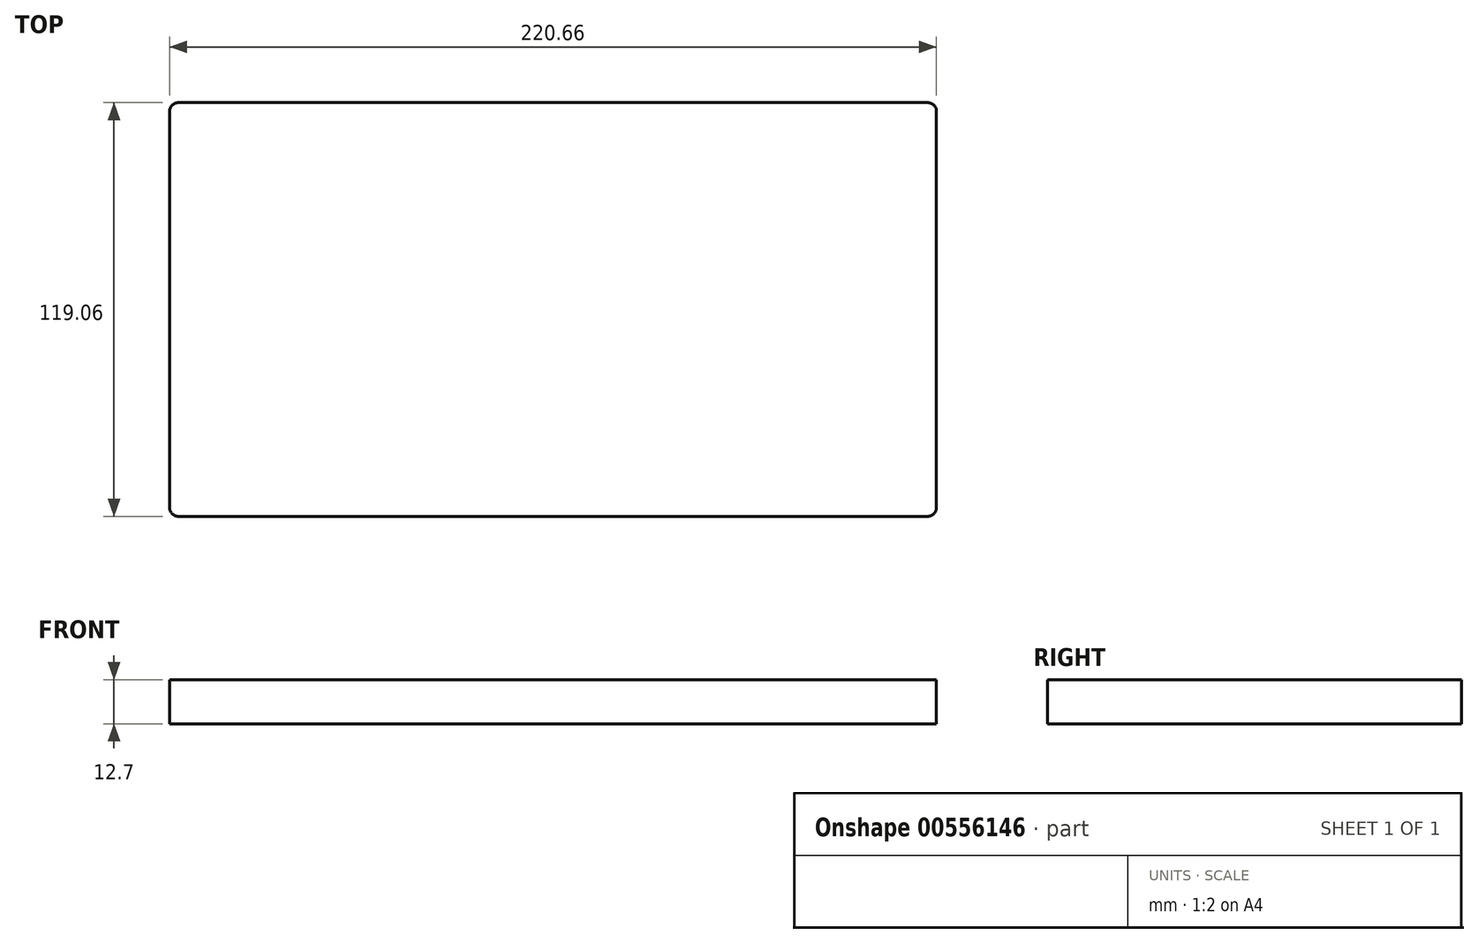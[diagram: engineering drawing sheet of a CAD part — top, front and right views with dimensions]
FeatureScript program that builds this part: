
annotation { "Feature Type Name" : "Feature", "Feature Type Description" : "" }
export const myFeature = defineFeature(function(context is Context, id is Id, definition is map)
    precondition{}
    {
        {
            var Q0;
            Q0=qCreatedBy(makeId("Top.planeOp"),FACE);
            var sketch = newSketch(context, id + "F0", { "sketchPlane" : qUnion([Q0])});
            skLineSegment(sketch, "E0.bottom", {"start": v(-107.79, 59.53) * mm, "end": v(107.79, 59.53) * mm});
            skLineSegment(sketch, "E0.top", {"start": v(-107.79, -59.53) * mm, "end": v(107.79, -59.53) * mm});
            skLineSegment(sketch, "E0.left", {"start": v(-110.33, 56.99) * mm, "end": v(-110.33, -56.99) * mm});
            skLineSegment(sketch, "E0.right", {"start": v(110.33, 56.99) * mm, "end": v(110.33, -56.99) * mm});
            skPoint(sketch, "E0.middle", {"position": v(0, 0) * mm});
            skPoint(sketch, "E1.visualSharp", {"position": v(-110.33, 59.53) * mm});
            skArc(sketch, "E1.filletArc", {"start": v(-107.79, 59.53) * mm, "mid": v(-109.59, 58.79) * mm, "end": v(-110.33, 56.99) * mm});
            skPoint(sketch, "E2.visualSharp", {"position": v(110.33, 59.53) * mm});
            skArc(sketch, "E2.filletArc", {"start": v(110.33, 56.99) * mm, "mid": v(109.59, 58.79) * mm, "end": v(107.79, 59.53) * mm});
            skPoint(sketch, "E3.visualSharp", {"position": v(110.33, -59.53) * mm});
            skArc(sketch, "E3.filletArc", {"start": v(107.79, -59.53) * mm, "mid": v(109.59, -58.79) * mm, "end": v(110.33, -56.99) * mm});
            skPoint(sketch, "E4.visualSharp", {"position": v(-110.33, -59.53) * mm});
            skArc(sketch, "E4.filletArc", {"start": v(-110.33, -56.99) * mm, "mid": v(-109.59, -58.79) * mm, "end": v(-107.79, -59.53) * mm});
            skSolve(sketch);
        }
        {
            var Q0;
            Q0=makeQuery(id+"F0.imprint","IMPRINT",FACE,{"disambiguationData":[TD([[makeQuery(id+"F0.imprint","IMPRINT",EDGE,{"derivedFrom":sQuery(id+"F0.wireOp",EDGE,"E0.bottom")}),-1.0]])]});
            extrude(context, id + "F1", {"entities" : qUnion([Q0]), "depth" : 12.7 * mm, "offsetDistance" : 25.4 * mm});
        }
    });
